# Revit family: HWB5_6 HandWashBasin
name_source: partatom
category: Plumbing Fixtures
units: mm (PartAtom-declared; Revit-internal decimal feet)

## family parameters
Always vertical = Yes
Cut with Voids When Loaded = No
Host = Wall
OmniClass Number = 23.45.00.00
OmniClass Title = Sanitary, Laundry, and Cleaning Equipment
Part Type = Normal
Room Calculation Point = No
Round Connector Dimension = Use Diameter
Shared = No

## types (2) — shared parameters
Assembly = Fabricated
Basin Material = Stainless Steel
Brand = Mercer
Description = Hand Wash Basin
Finish = Satin
Includes = Low Profile Trap
Logo Material = Paint Black
Material = 1.2mm 304 grade Stainless Steel
Model = HWB5 & 6
Rad = 160 mm  [stored 0.524934 ft]
Waste = Flat 40mm outlet
zero-valued in all types: Default Elevation

## per-type parameters (varying)
| type | Basin U/S | Bottom | Depth | Manufacturer |
| HWB5 | 325 mm | 237 mm | 350 mm  [stored 1.14829 ft] |  |
| HWB6 | 375 mm  [stored 1.23031 ft] | 287 mm | 400 mm  [stored 1.31234 ft] | Mercer |

note: [stored X ft] marks values corroborated as IEEE doubles in the binary element streams (Revit-internal decimal feet)

## geometry (parser evidence)
native form markers: Sweep x5
no freeform markers — native parametric forms only
